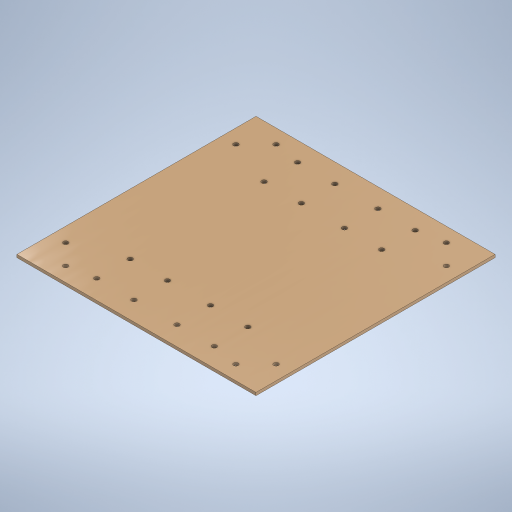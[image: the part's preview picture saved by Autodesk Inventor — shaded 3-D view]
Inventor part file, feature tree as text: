
AUTODESK INVENTOR PART (.ipt)
format: ipt  version: 2024 (Build 280153000, 153)  size: 305,152 bytes
history: native  units: in
note: dims shown in document units (in); Inventor stores cm internally (conversion verified against a paired STEP export)
features: sketch x3, hole x2, other x1, extrude x1
ambient origin geometry x8: Origin, YZ Plane, XZ Plane, XY Plane, X Axis, Y Axis, Z Axis, Center Point
bodies: Body1 (feature_tree)
feature tree (7):
  other  "Main Body"
  extrude  "Main Body Extrusion"  Depth=0.3937in
  hole  "Bracket Holes"  [1 undecoded]
  hole  "Hole4"  [1 undecoded]
  sketch  "Sketch3"  dims[d86=9.8425in d87=9.8425in d88=0.1969in d89=0.2953in d90=0.1476in d91=0.0984in d92=90.0deg d93=0.3937in d94=0.8108in d95=1.1811in]
  sketch  "Sketch11"  dims[d96=1.1811in d97=0.7874in]
  sketch  "Sketch12"  dims[d98=0.7874in d99=0.3937in d100=0.3937in d101=0.1575in d102=0.1969in d103=0.1969in d104=0.1575in d105=1.5748in d107=360.0deg d109=0.1969in d110=0.2953in d111=0.1476in d112=0.0984in d113=90.0deg d114=0.3937in d115=0.8108in d38=0.0394in d39=0.0394in d40=0.0394in d41=0.0059in d42=0.0098in d43=0.0148in d44=32.2835in d45=0.0295in d46=46.4567in d47=0.0025in d48=0.0295in d49=0.0148in d65=0.1969in d66=1.9685in d67=0.1969in d68=1.9685in]
note: 2 required parameter values undecoded (feature->parameter linkage not recoverable at this tier; creation-order binding heuristic only, values carry confidence <= 0.55)
